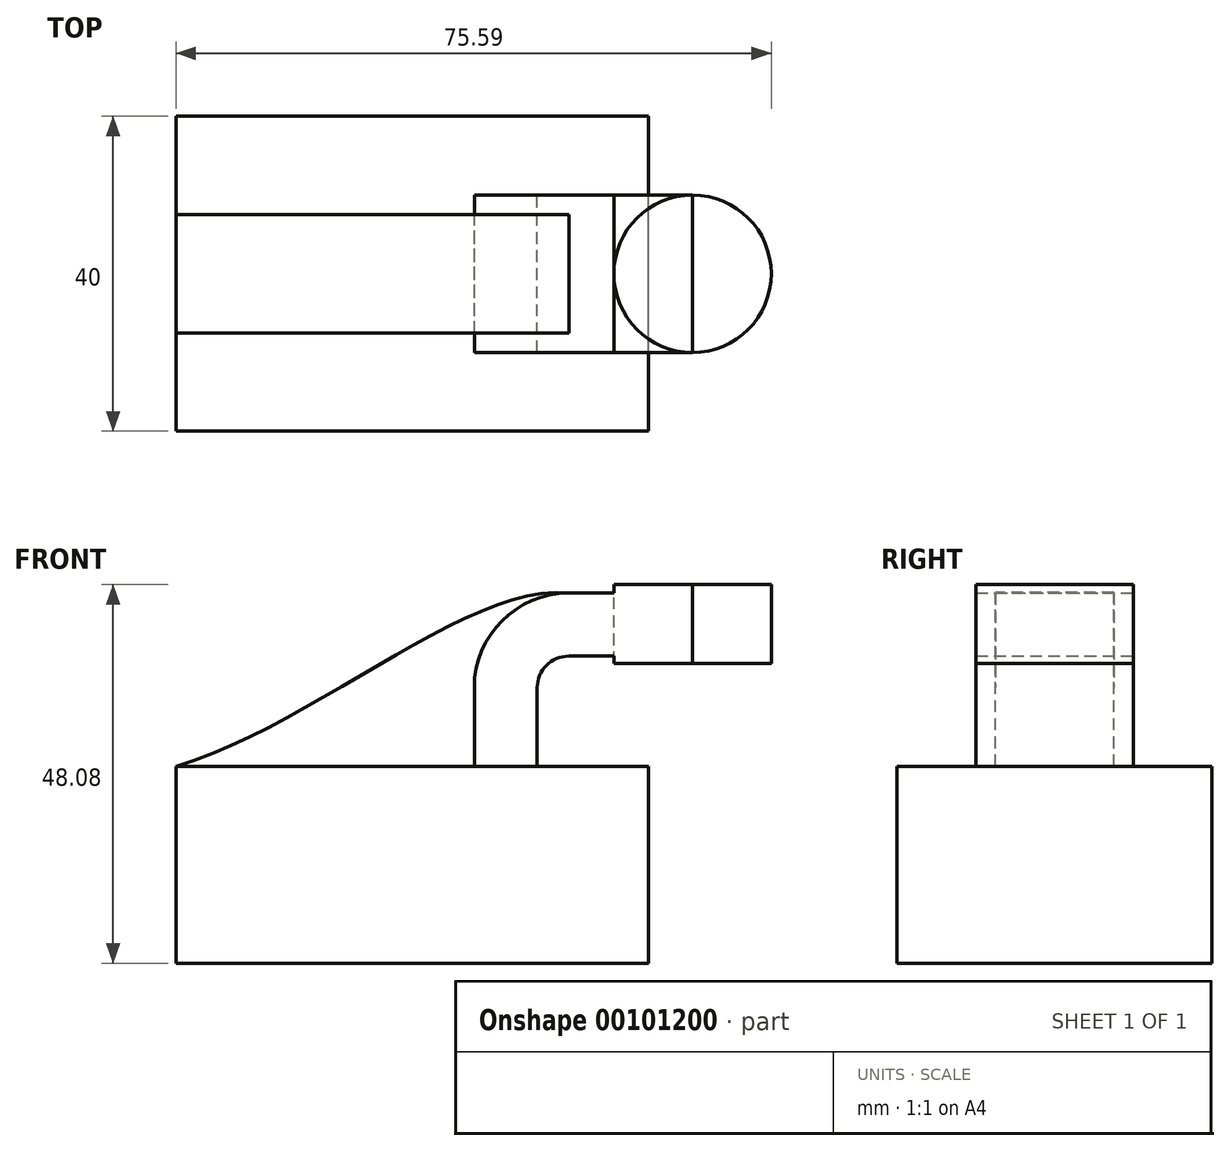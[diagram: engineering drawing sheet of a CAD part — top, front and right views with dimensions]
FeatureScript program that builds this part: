
annotation { "Feature Type Name" : "Feature", "Feature Type Description" : "" }
export const myFeature = defineFeature(function(context is Context, id is Id, definition is map)
    precondition{}
    {
        {
            var Q0;
            Q0=qCreatedBy(makeId("Front.planeOp"),FACE);
            var sketch = newSketch(context, id + "F0", { "sketchPlane" : qUnion([Q0])});
            skLineSegment(sketch, "E0.bottom", {"start": v(30, -12.5) * mm, "end": v(-30, -12.5) * mm});
            skLineSegment(sketch, "E0.top", {"start": v(30, 12.5) * mm, "end": v(-30, 12.5) * mm});
            skLineSegment(sketch, "E0.left", {"start": v(30, -12.5) * mm, "end": v(30, 12.5) * mm});
            skLineSegment(sketch, "E0.right", {"start": v(-30, -12.5) * mm, "end": v(-30, 12.5) * mm});
            skPoint(sketch, "E0.middle", {"position": v(0, 0) * mm});
            skLineSegment(sketch, "E1.bottom", {"start": v(45.6, 25.58) * mm, "end": v(25.6, 25.58) * mm});
            skLineSegment(sketch, "E1.top", {"start": v(45.6, 35.58) * mm, "end": v(25.6, 35.58) * mm});
            skLineSegment(sketch, "E1.left", {"start": v(45.6, 25.58) * mm, "end": v(45.6, 35.58) * mm});
            skLineSegment(sketch, "E1.right", {"start": v(25.6, 25.58) * mm, "end": v(25.6, 35.58) * mm});
            skPoint(sketch, "E1.middle", {"position": v(35.6, 30.58) * mm});
            skLineSegment(sketch, "E2", {"start": v(15.87, 12.5) * mm, "end": v(15.87, 22.5) * mm});
            skArc(sketch, "E3", {"start": v(19.87, 26.5) * mm, "mid": v(17.04, 25.33) * mm, "end": v(15.87, 22.5) * mm});
            skLineSegment(sketch, "E4", {"start": v(19.87, 26.5) * mm, "end": v(35.56, 26.5) * mm});
            skLineSegment(sketch, "E5.0", {"start": v(19.87, 34.5) * mm, "end": v(35.56, 34.5) * mm});
            skArc(sketch, "E5.1", {"start": v(19.87, 34.5) * mm, "mid": v(11.39, 30.99) * mm, "end": v(7.87, 22.5) * mm});
            skLineSegment(sketch, "E5.2", {"start": v(7.87, 12.5) * mm, "end": v(7.87, 22.5) * mm});
            skFitSpline(sketch, "E6", {"points": [v(-30, 12.5) * mm, v(19.87, 34.5) * mm], "startDerivative": vector(52.8, 15.62) * mm, "endDerivative": vector(37.88, -4.4) * mm});
            skLineSegment(sketch, "E7", {"start": v(35.6, 35.58) * mm, "end": v(35.6, 25.58) * mm});
            skSolve(sketch);
        }
        {
            var Q0;
            Q0=makeQuery(id+"F0.imprint","IMPRINT",FACE,{"disambiguationData":[TD([[makeQuery(id+"F0.imprint","IMPRINT",EDGE,{"derivedFrom":sQuery(id+"F0.wireOp",EDGE,"E0.bottom")}),-1.0]])]});
            extrude(context, id + "F1", {"entities" : qUnion([Q0]), "endBound" : BoundingType.SYMMETRIC, "depth" : 40 * mm});
        }
        {
            var Q0;
            {var subQ2=sQuery(id+"F0.wireOp",EDGE,"E2");Q0=makeQuery(id+"F0.imprint","IMPRINT",FACE,{"disambiguationData":[TD([[makeQuery(id+"F0.imprint","IMPRINT",EDGE,{"derivedFrom":subQ2}),1.0]])]});}
            var Q1;
            {var subQ7=sQuery(id+"F0.wireOp",EDGE,"E7");Q1=makeQuery(id+"F0.imprint","IMPRINT",FACE,{"disambiguationData":[TD([[makeQuery(id+"F0.imprint","IMPRINT",EDGE,{"derivedFrom":subQ7}),-1.0]])]});}
            extrude(context, id + "F2", {"entities" : qUnion([Q0, Q1]), "endBound" : BoundingType.SYMMETRIC, "depth" : 20 * mm});
        }
        {
            var Q0;
            Q0=makeQuery(id+"F0.imprint","IMPRINT",FACE,{"disambiguationData":[TD([[makeQuery(id+"F0.imprint","IMPRINT",EDGE,{"derivedFrom":sQuery(id+"F0.wireOp",EDGE,"E5.1")}),-1.0]])]});
            extrude(context, id + "F3", {"entities" : qUnion([Q0]), "endBound" : BoundingType.SYMMETRIC, "depth" : 15 * mm});
        }
        {
            var Q0;
            {var subQ0=sQuery(id+"F0.wireOp",EDGE,"E1.left");Q0=makeQuery(id+"F0.imprint","IMPRINT",FACE,{"disambiguationData":[TD([[makeQuery(id+"F0.imprint","IMPRINT",EDGE,{"derivedFrom":subQ0}),1.0]])]});}
            var Q1;
            Q1=sQuery(id+"F0.wireOp",EDGE,"E7");
            revolve(context, id + "F4", {"entities" : qUnion([Q0]), "axis" : qUnion([Q1]), "revolveType" : RevolveType.FULL});
        }
    });
